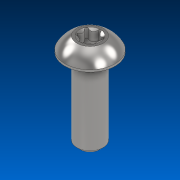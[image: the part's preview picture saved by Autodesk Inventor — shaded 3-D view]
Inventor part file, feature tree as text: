
AUTODESK INVENTOR PART (.ipt)
format: ipt  version: 2022.2 (Build 262287000, 287)  size: 184,320 bytes
history: native  units: in
note: dims shown in document units (in); Inventor stores cm internally (conversion verified against a paired STEP export)
features: direct_edit x1, chamfer x1, move_body x1
ambient origin geometry x8: Origin, YZ Plane, XZ Plane, XY Plane, X Axis, Y Axis, Z Axis, Center Point
bodies: Solid1 (feature_tree)
feature tree (3):
  direct_edit  "Direct Edit1"
  chamfer  "Chamfer2"  [1 undecoded]
  move_body  "Move1"
note: 1 required parameter value undecoded (feature->parameter linkage not recoverable at this tier; creation-order binding heuristic only, values carry confidence <= 0.55)
